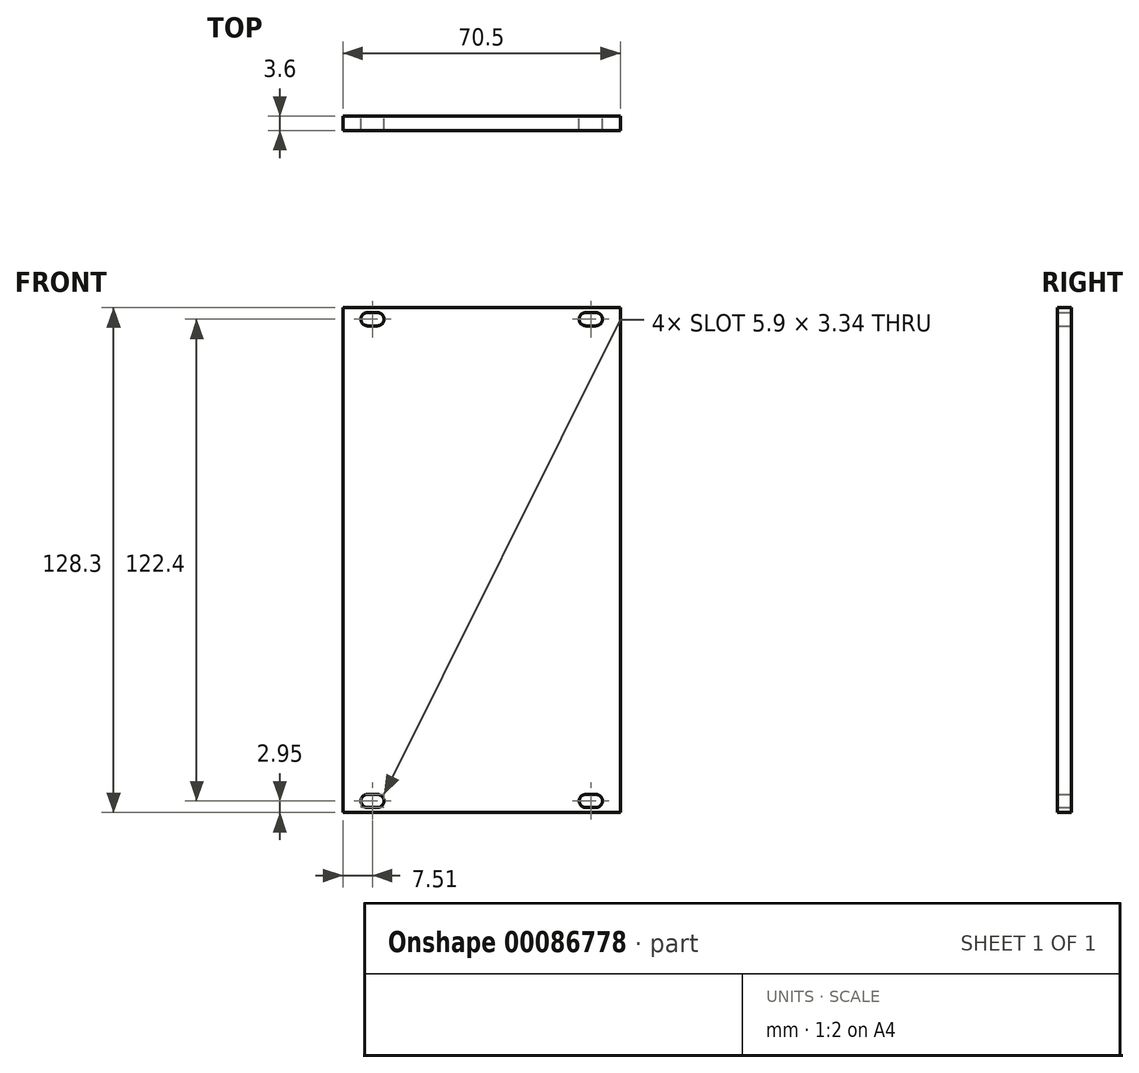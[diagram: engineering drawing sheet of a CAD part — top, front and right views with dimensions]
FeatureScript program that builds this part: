
annotation { "Feature Type Name" : "Feature", "Feature Type Description" : "" }
export const myFeature = defineFeature(function(context is Context, id is Id, definition is map)
    precondition{}
    {
        {
            var Q0;
            Q0=qCreatedBy(makeId("Front.planeOp"),FACE);
            var sketch = newSketch(context, id + "F0", { "sketchPlane" : qUnion([Q0])});
            skLineSegment(sketch, "E0.bottom", {"start": v(35.25, 64.15) * mm, "end": v(-35.25, 64.15) * mm});
            skLineSegment(sketch, "E0.top", {"start": v(35.25, -64.15) * mm, "end": v(-35.25, -64.15) * mm});
            skLineSegment(sketch, "E0.left", {"start": v(35.25, 64.15) * mm, "end": v(35.25, -64.15) * mm});
            skLineSegment(sketch, "E0.right", {"start": v(-35.25, 64.15) * mm, "end": v(-35.25, -64.15) * mm});
            skPoint(sketch, "E0.middle", {"position": v(0, 0) * mm});
            skArc(sketch, "E1", {"start": v(-29.02, 62.87) * mm, "mid": v(-30.7, 61.2) * mm, "end": v(-29.02, 59.53) * mm});
            skArc(sketch, "E2", {"start": v(-26.46, 59.53) * mm, "mid": v(-24.8, 61.2) * mm, "end": v(-26.46, 62.87) * mm});
            skLineSegment(sketch, "E3", {"start": v(-29.02, 62.87) * mm, "end": v(-26.46, 62.87) * mm});
            skLineSegment(sketch, "E4", {"start": v(-29.02, 59.53) * mm, "end": v(-26.46, 59.53) * mm});
            skLineSegment(sketch, "E5.MirrorCS", {"start": v(29.02, 62.87) * mm, "end": v(26.46, 62.87) * mm});
            skArc(sketch, "E6.MirrorCS", {"start": v(29.02, 62.87) * mm, "mid": v(30.7, 61.2) * mm, "end": v(29.02, 59.53) * mm});
            skLineSegment(sketch, "E7.MirrorCS", {"start": v(29.02, 59.53) * mm, "end": v(26.46, 59.53) * mm});
            skArc(sketch, "E8.MirrorCS", {"start": v(26.46, 59.53) * mm, "mid": v(24.8, 61.2) * mm, "end": v(26.46, 62.87) * mm});
            skArc(sketch, "E9.MirrorCS", {"start": v(-29.02, -62.87) * mm, "mid": v(-30.7, -61.2) * mm, "end": v(-29.02, -59.53) * mm});
            skLineSegment(sketch, "E10.MirrorCS", {"start": v(-29.02, -62.87) * mm, "end": v(-26.46, -62.87) * mm});
            skArc(sketch, "E11.MirrorCS", {"start": v(-26.46, -59.53) * mm, "mid": v(-24.8, -61.2) * mm, "end": v(-26.46, -62.87) * mm});
            skLineSegment(sketch, "E12.MirrorCS", {"start": v(-29.02, -59.53) * mm, "end": v(-26.46, -59.53) * mm});
            skArc(sketch, "E13.MirrorCS", {"start": v(26.46, -59.53) * mm, "mid": v(24.8, -61.2) * mm, "end": v(26.46, -62.87) * mm});
            skLineSegment(sketch, "E14.MirrorCS", {"start": v(29.02, -62.87) * mm, "end": v(26.46, -62.87) * mm});
            skArc(sketch, "E15.MirrorCS", {"start": v(29.02, -62.87) * mm, "mid": v(30.7, -61.2) * mm, "end": v(29.02, -59.53) * mm});
            skLineSegment(sketch, "E16.MirrorCS", {"start": v(29.02, -59.53) * mm, "end": v(26.46, -59.53) * mm});
            skSolve(sketch);
        }
        {
            var Q0;
            Q0=makeQuery(id+"F0.imprint","IMPRINT",FACE,{"disambiguationData":[TD([[makeQuery(id+"F0.imprint","IMPRINT",EDGE,{"derivedFrom":sQuery(id+"F0.wireOp",EDGE,"E0.bottom")}),1.0]])]});
            extrude(context, id + "F1", {"entities" : qUnion([Q0]), "depth" : 3.6 * mm});
        }
    });
